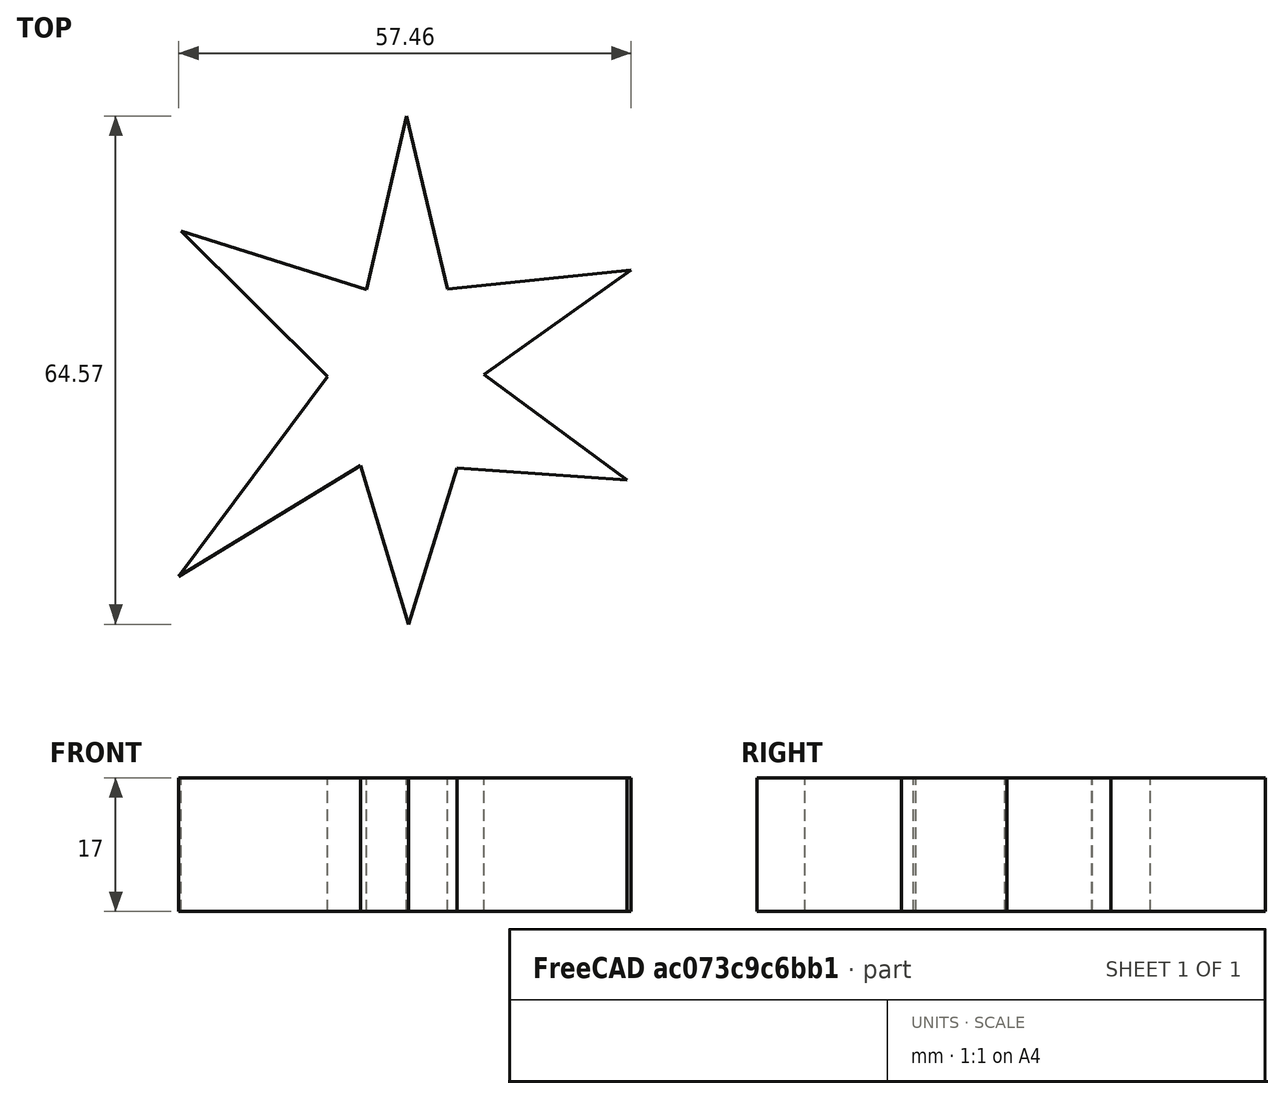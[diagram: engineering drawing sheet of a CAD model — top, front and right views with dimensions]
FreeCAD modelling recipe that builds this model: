
FCSTD DOCUMENT  (FreeCAD 0.21R33771 (Git))
Label: OJT1_T16P01_extrusio_estgrella
License: All rights reserved
LicenseURL: http://en.wikipedia.org/wiki/All_rights_reserved
objects: Sketcher::SketchObject×1, PartDesign::Pad×1, PartDesign::Body×1
note: 4 computed .brp shape members not serialized (recipe doc carries the construction recipe); baked Part::Feature solids carry a one-line shape summary decoded from their .brp

FEATURE [Sketcher::SketchObject] Sketch001  label="Sketch_star"
  FullyConstrained = false
  MapMode = 5
  Support = -> [XY_Plane]
  sketch-geometry (12):
    g0: LineSegment StartX=0.015784 StartY=40.0813 StartZ=0 EndX=5.22222 EndY=18.0948 EndZ=0
    g1: LineSegment StartX=5.22222 StartY=18.0948 StartZ=0 EndX=28.5459 EndY=20.4815 EndZ=0
    g2: LineSegment StartX=28.5459 StartY=20.4815 StartZ=0 EndX=9.86975 EndY=7.26008 EndZ=0
    g3: LineSegment StartX=9.86975 StartY=7.26008 StartZ=0 EndX=28.0138 EndY=-6.14681 EndZ=0
    g4: LineSegment StartX=28.0138 StartY=-6.14681 StartZ=0 EndX=6.42413 EndY=-4.61155 EndZ=0
    g5: LineSegment StartX=6.42413 StartY=-4.61155 StartZ=0 EndX=0.28961 EndY=-24.4882 EndZ=0
    g6: LineSegment StartX=0.28961 StartY=-24.4882 StartZ=0 EndX=-5.83185 EndY=-4.29497 EndZ=0
    g7: LineSegment StartX=-5.83185 StartY=-4.29497 StartZ=0 EndX=-28.9101 EndY=-18.4033 EndZ=0
    g8: LineSegment StartX=-28.9101 StartY=-18.4033 StartZ=0 EndX=-9.99274 EndY=6.97222 EndZ=0
    g9: LineSegment StartX=-9.99274 StartY=6.97222 StartZ=0 EndX=-28.6361 EndY=25.4627 EndZ=0
    g10: LineSegment StartX=-28.6361 StartY=25.4627 StartZ=0 EndX=-5.06921 EndY=18.0163 EndZ=0
    g11: LineSegment StartX=-5.06921 StartY=18.0163 StartZ=0 EndX=0.015784 EndY=40.0813 EndZ=0
  constraints (11):
    c: Coincident(g0,g1)
    c: Coincident(g1,g2)
    c: Coincident(g2,g3)
    c: Coincident(g3,g4)
    c: Coincident(g4,g5)
    c: Coincident(g5,g6)
    c: Coincident(g6,g7)
    c: Coincident(g7,g8)
    c: Coincident(g8,g9)
    c: Coincident(g9,g10)
    c: Coincident(g10,g11)
FEATURE [PartDesign::Pad] Pad  label="star"
  Direction = (0,0,1)
  Length = 17
  Length2 = 10
  Profile = -> Sketch001
  ReferenceAxis = -> Sketch001 [N_Axis]
  Type = 0
FEATURE [PartDesign::Body] Body  label="body"
  Group = -> [Sketch001,Pad]
  Origin = -> Origin
  Tip = -> Pad
